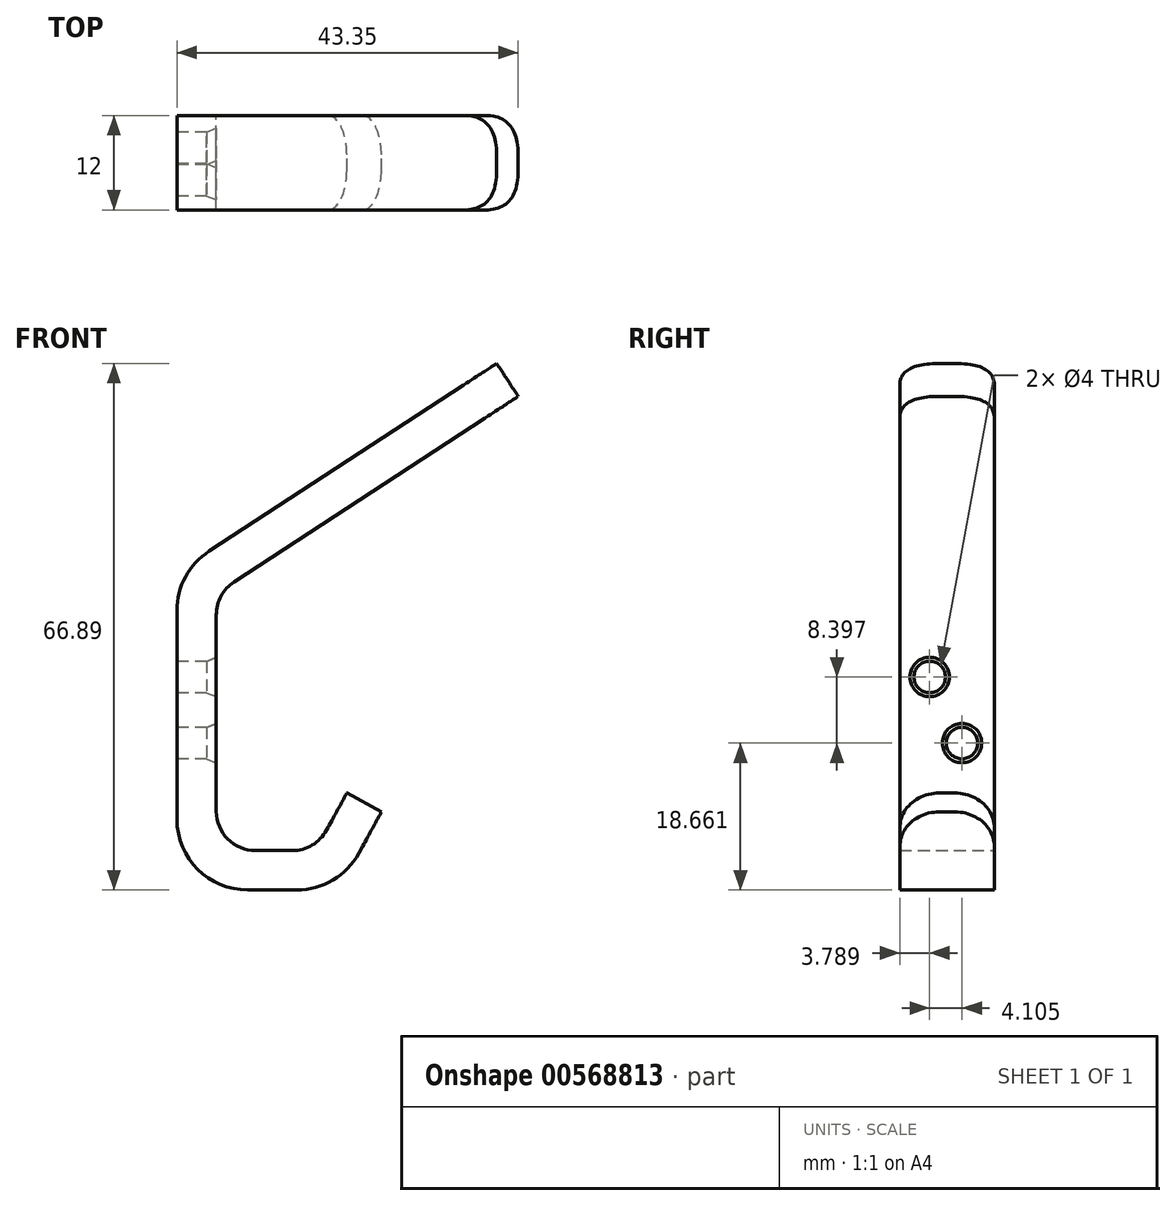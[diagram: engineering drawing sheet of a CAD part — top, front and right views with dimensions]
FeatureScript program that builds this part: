
annotation { "Feature Type Name" : "Feature", "Feature Type Description" : "" }
export const myFeature = defineFeature(function(context is Context, id is Id, definition is map)
    precondition{}
    {
        {
            var Q0;
            Q0=qCreatedBy(makeId("Front.planeOp"),FACE);
            var sketch = newSketch(context, id + "F0", { "sketchPlane" : qUnion([Q0])});
            skLineSegment(sketch, "E0", {"start": v(0, 0) * mm, "end": v(0, 40.37) * mm});
            skLineSegment(sketch, "E1", {"start": v(0, 40.37) * mm, "end": v(40.62, 66.89) * mm});
            skLineSegment(sketch, "E2", {"start": v(0, 0) * mm, "end": v(20.56, 0) * mm});
            skLineSegment(sketch, "E3", {"start": v(20.56, 0) * mm, "end": v(25.97, 9.92) * mm});
            skLineSegment(sketch, "E4", {"start": v(25.97, 9.92) * mm, "end": v(21.58, 12.32) * mm});
            skPoint(sketch, "E5.endSnap0", {"position": v(0, 20.19) * mm});
            skPoint(sketch, "E6.orphan", {"position": v(-8.55, 9.92) * mm});
            skPoint(sketch, "E7.end.orphan", {"position": v(-8.55, -0.53) * mm});
            skPoint(sketch, "E8.end.orphan", {"position": v(19.81, 3.95) * mm});
            skPoint(sketch, "E5.end.orphan", {"position": v(6.16, 20.19) * mm});
            skPoint(sketch, "E5.start.orphan", {"position": v(0, 20.19) * mm});
            skLineSegment(sketch, "E9.0", {"start": v(5, 37.66) * mm, "end": v(43.35, 62.7) * mm});
            skLineSegment(sketch, "E9.1", {"start": v(5, 5) * mm, "end": v(5, 37.66) * mm});
            skLineSegment(sketch, "E10.0", {"start": v(5, 5) * mm, "end": v(18.47, 5) * mm});
            skLineSegment(sketch, "E11.0", {"start": v(17.6, 5) * mm, "end": v(21.58, 12.32) * mm});
            skPoint(sketch, "E12.orphan", {"position": v(19.81, 13.28) * mm});
            skLineSegment(sketch, "E13", {"start": v(40.62, 66.89) * mm, "end": v(43.35, 62.7) * mm});
            skSolve(sketch);
        }
        {
            var Q0;
            Q0=makeQuery(id+"F0.imprint","IMPRINT",FACE,{"disambiguationData":[TD([[makeQuery(id+"F0.imprint","IMPRINT",EDGE,{"derivedFrom":sQuery(id+"F0.wireOp",EDGE,"E0")}),-1.0]])]});
            extrude(context, id + "F1", {"entities" : qUnion([Q0]), "depth" : 12 * mm});
        }
        {
            var Q0;
            Q0=makeQuery(id+"F1.opExtrude","SWEPT_EDGE",EDGE,{"disambiguationData":[OSD([sQuery(id+"F0.wireOp",EDGE,"E2"),sQuery(id+"F0.wireOp",EDGE,"E3")])]});
            fillet(context, id + "F2", {"entities" : qUnion([Q0]), "radius" : 9 * mm, "tangentPropagation" : true, "allowEdgeOverflow" : false});
        }
        {
            var Q0;
            Q0=makeQuery(id+"F1.opExtrude","SWEPT_EDGE",EDGE,{"disambiguationData":[OSD([sQuery(id+"F0.wireOp",EDGE,"E10.0"),sQuery(id+"F0.wireOp",EDGE,"E11.0")])]});
            fillet(context, id + "F3", {"entities" : qUnion([Q0]), "radius" : 5 * mm, "tangentPropagation" : true, "allowEdgeOverflow" : false});
        }
        {
            var Q0;
            Q0=makeQuery(id+"F1.opExtrude","SWEPT_EDGE",EDGE,{"disambiguationData":[OSD([sQuery(id+"F0.wireOp",EDGE,"E0"),sQuery(id+"F0.wireOp",EDGE,"E1")])]});
            fillet(context, id + "F4", {"entities" : qUnion([Q0]), "radius" : 9 * mm, "tangentPropagation" : true, "allowEdgeOverflow" : false});
        }
        {
            var Q0;
            Q0=makeQuery(id+"F1.opExtrude","SWEPT_EDGE",EDGE,{"disambiguationData":[OSD([sQuery(id+"F0.wireOp",EDGE,"E9.0"),sQuery(id+"F0.wireOp",EDGE,"E9.1")])]});
            fillet(context, id + "F5", {"entities" : qUnion([Q0]), "radius" : 5 * mm, "tangentPropagation" : true, "allowEdgeOverflow" : false});
        }
        {
            var Q0;
            Q0=makeQuery(id+"F1.opExtrude","CAP_EDGE",EDGE,{"disambiguationData":[OSD([sQuery(id+"F0.wireOp",EDGE,"E4")])],"isStart":false});
            fillet(context, id + "F6", {"entities" : qUnion([Q0]), "radius" : 5 * mm, "tangentPropagation" : true, "allowEdgeOverflow" : false});
        }
        {
            var Q0;
            Q0=makeQuery(id+"F1.opExtrude","CAP_EDGE",EDGE,{"disambiguationData":[OSD([sQuery(id+"F0.wireOp",EDGE,"E4")])],"isStart":true});
            fillet(context, id + "F7", {"entities" : qUnion([Q0]), "radius" : 5 * mm, "tangentPropagation" : true, "allowEdgeOverflow" : false});
        }
        {
            var Q0;
            Q0=makeQuery(id+"F1.opExtrude","CAP_EDGE",EDGE,{"disambiguationData":[OSD([sQuery(id+"F0.wireOp",EDGE,"E13")])],"isStart":false});
            var Q1;
            Q1=makeQuery(id+"F1.opExtrude","CAP_EDGE",EDGE,{"disambiguationData":[OSD([sQuery(id+"F0.wireOp",EDGE,"E13")])],"isStart":true});
            fillet(context, id + "F8", {"entities" : qUnion([Q0, Q1]), "radius" : 5 * mm, "tangentPropagation" : true, "rho" : .5, "crossSection" : FilletCrossSection.CONIC, "allowEdgeOverflow" : false});
        }
        {
            var Q0;
            Q0=makeQuery(id+"F1.opExtrude","SWEPT_FACE",FACE,{"disambiguationData":[OSD([sQuery(id+"F0.wireOp",EDGE,"E9.1")])]});
            var sketch = newSketch(context, id + "F9", { "sketchPlane" : qUnion([Q0])});
            skSolve(sketch);
        }
        {
            var Q0;
            Q0=makeQuery(id+"F1.opExtrude","SWEPT_EDGE",EDGE,{"disambiguationData":[OSD([sQuery(id+"F0.wireOp",EDGE,"E9.1"),sQuery(id+"F0.wireOp",EDGE,"E10.0")])]});
            fillet(context, id + "F10", {"entities" : qUnion([Q0]), "radius" : 5 * mm, "tangentPropagation" : true, "allowEdgeOverflow" : false});
        }
        {
            var Q0;
            Q0=makeQuery(id+"F1.opExtrude","SWEPT_EDGE",EDGE,{"disambiguationData":[OSD([sQuery(id+"F0.wireOp",EDGE,"E0"),sQuery(id+"F0.wireOp",EDGE,"E2")])]});
            fillet(context, id + "F11", {"entities" : qUnion([Q0]), "radius" : 9 * mm, "tangentPropagation" : true, "allowEdgeOverflow" : false});
        }
        {
            var Q0;
            {var subQ0=sQuery(id+"F0.wireOp",EDGE,"E9.1");Q0=makeQuery(id+"F9.imprint","IMPRINT",FACE,{"disambiguationData":[TD([[makeQuery(id+"F9.imprint","IMPRINT",EDGE,{"derivedFrom":makeQuery(id+"F1.opExtrude","CAP_EDGE",EDGE,{"disambiguationData":[OSD([subQ0])],"isStart":true})}),1.0]])]});}
            var sketch = newSketch(context, id + "F12", { "sketchPlane" : qUnion([Q0])});
            skCircle(sketch, "E14", {"center": v(-8.21, 27.06) * mm, "radius": 2.18 * mm});
            skCircle(sketch, "E15", {"center": v(-4.1, 18.66) * mm, "radius": 2.34 * mm});
            skSolve(sketch);
        }
        {
            var Q0;
            Q0=sQuery(id+"F12.wireOp",VERTEX,"E14.center");
            var Q1;
            Q1=makeQuery(id+"F1.opExtrude","SWEPT_BODY",BODY,{"disambiguationData":[OSD([sQuery(id+"F0.wireOp",EDGE,"E0"),sQuery(id+"F0.wireOp",EDGE,"E1"),sQuery(id+"F0.wireOp",EDGE,"E2"),sQuery(id+"F0.wireOp",EDGE,"E3"),sQuery(id+"F0.wireOp",EDGE,"E4"),sQuery(id+"F0.wireOp",EDGE,"E9.0"),sQuery(id+"F0.wireOp",EDGE,"E9.1"),sQuery(id+"F0.wireOp",EDGE,"E10.0"),sQuery(id+"F0.wireOp",EDGE,"E11.0"),sQuery(id+"F0.wireOp",EDGE,"E13")])]});
            hole(context, id + "F13", {"style" : HoleStyle.C_SINK, "endStyle" : HoleEndStyle.THROUGH, "holeDiameter" : 4 * mm, "cSinkDiameter" : 5 * mm, "cSinkAngle" : 45 * degree, "isTappedThrough" : true, "tappedDepth" : 12 * mm, "tapClearance" : 3, "locations" : qUnion([Q0]), "scope" : qUnion([Q1]), "startStyle" : HoleStartStyle.PART});
        }
        {
            var Q0;
            Q0=sQuery(id+"F12.wireOp",VERTEX,"E15.center");
            var Q1;
            Q1=makeQuery(id+"F1.opExtrude","SWEPT_BODY",BODY,{"disambiguationData":[OSD([sQuery(id+"F0.wireOp",EDGE,"E0"),sQuery(id+"F0.wireOp",EDGE,"E1"),sQuery(id+"F0.wireOp",EDGE,"E2"),sQuery(id+"F0.wireOp",EDGE,"E3"),sQuery(id+"F0.wireOp",EDGE,"E4"),sQuery(id+"F0.wireOp",EDGE,"E9.0"),sQuery(id+"F0.wireOp",EDGE,"E9.1"),sQuery(id+"F0.wireOp",EDGE,"E10.0"),sQuery(id+"F0.wireOp",EDGE,"E11.0"),sQuery(id+"F0.wireOp",EDGE,"E13")])]});
            hole(context, id + "F14", {"style" : HoleStyle.C_SINK, "endStyle" : HoleEndStyle.THROUGH, "holeDiameter" : 4 * mm, "cSinkDiameter" : 5 * mm, "cSinkAngle" : 45 * degree, "isTappedThrough" : true, "tappedDepth" : 12 * mm, "tapClearance" : 3, "locations" : qUnion([Q0]), "scope" : qUnion([Q1]), "startStyle" : HoleStartStyle.PART});
        }
    });
